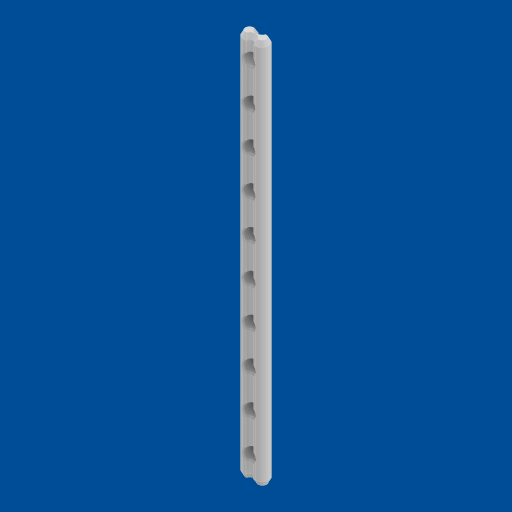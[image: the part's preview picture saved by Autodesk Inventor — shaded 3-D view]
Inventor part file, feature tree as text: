
AUTODESK INVENTOR PART (.ipt)
format: ipt  version: 2023 (Build 270158000, 158)  size: 248,320 bytes
history: native  units: mm
features: chamfer x8, extrude x2, sketch x2
ambient origin geometry x8: Origin, YZ Plane, XZ Plane, XY Plane, X Axis, Y Axis, Z Axis, Center Point
bodies: Solid1 (feature_tree)
feature tree (12):
  extrude  "Extrusion1"  Depth=11.0mm
  chamfer  "Chamfer1"  Distance=15.0mm
  chamfer  "Chamfer2"  Distance=6.5mm
  chamfer  "Chamfer3"  Distance=325.0mm
  chamfer  "Chamfer4"  Distance=2.0mm Angle=30.0deg
  chamfer  "Chamfer5"  Distance=2.0mm Angle=30.0deg
  chamfer  "Chamfer6"  Distance=2.0mm Angle=30.0deg
  chamfer  "Chamfer7"  Distance=2.0mm Angle=30.0deg
  chamfer  "Chamfer8"  Distance=2.0mm Angle=30.0deg
  extrude  "Extrusion2"  Depth=10.0mm TaperAngle=30.0deg
  sketch  "Sketch1"  dims[d0=11.0mm d1=11.0mm]
  sketch  "Sketch2"  dims[d2=15.0mm d3=15.0mm d4=6.5mm d5=325.0mm d6=0.0mm d7=2.0mm d8=4.0mm d9=30.0deg d10=2.0mm d11=4.0mm d12=30.0deg d13=2.0mm d14=4.0mm d15=30.0deg d16=2.0mm d17=4.0mm d18=30.0deg d19=2.0mm d20=4.0mm d21=30.0deg d22=4.0mm d23=2.0mm d24=30.0deg d25=4.0mm d26=2.0mm d27=30.0deg d28=4.0mm d29=2.0mm d30=30.0deg d31=15.0mm d32=11.0mm d33=100.0mm d35=32.0mm d36=10.0mm d38=10.0mm d40=20.0mm d41=0.0mm]
